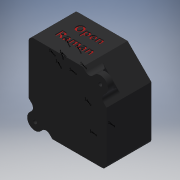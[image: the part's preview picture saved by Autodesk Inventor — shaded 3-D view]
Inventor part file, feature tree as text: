
AUTODESK INVENTOR PART (.ipt)
format: ipt  version: 2017 (Build 210142000, 142)  size: 787,968 bytes
history: native  units: mm
features: sketch x12, extrude x11, other x6, fillet x5, hole x4, projected_geometry x3, chamfer x2
ambient origin geometry x8: Origin, YZ Plane, XZ Plane, XY Plane, X Axis, Y Axis, Z Axis, Center Point
bodies: Body1 (feature_tree)
feature tree (43):
  other  "Blocks"
  other  "OTICA"
  sketch  "Sketch7"  dims[d1=25.4mm d25=0.685475mm]
  extrude  "Extrusion8"  Depth=0.685475mm
  extrude  "Extrusion9"  TaperAngle=112.5deg  [1 undecoded]
  extrude  "Extrusion10"  Depth=10.0mm
  hole  "Hole2"  [1 undecoded]
  extrude  "Extrusion15"  Depth=12.212069mm
  extrude  "Extrusion11"  Depth=11.349876mm
  fillet  "Fillet1"  Radius=10.236356mm
  hole  "Hole3"  [1 undecoded]
  chamfer  "Chamfer1"  Distance=3.154683mm
  hole  "Hole4"  [1 undecoded]
  fillet  "Fillet2"  Radius=20.0mm
  sketch  "Sketch13"  dims[d183=13.325589mm d184=11.349876mm d185=10.236356mm]
  extrude  "Extrusion12"  Depth=10.0mm
  extrude  "Extrusion13"  Depth=10.0mm
  extrude  "Extrusion14"  Depth=10.0mm
  fillet  "Fillet3"  Radius=13.0mm
  extrude  "Extrusion16"  Depth=10.0mm
  extrude  "Extrusion17"  Depth=10.0mm
  fillet  "Fillet4"  Radius=3.529965mm
  fillet  "Fillet5"  Radius=1.293324mm
  extrude  "Extrusion18"  Depth=10.0mm
  chamfer  "Chamfer2"  Angle=90.0deg  [1 undecoded]
  hole  "Hole5"  [1 undecoded]
  other  "PENTAPRISMA"
  other  "PRISMA.ENTRADA"
  sketch  "Sketch8"  dims[d100=3.368863mm d105=3.368863mm d106=6.737727mm d114=90.0deg d115=112.5deg d116=112.5deg d117=112.5deg]
  sketch  "Sketch9"  dims[d118=15.0mm]
  sketch  "Sketch10"  dims[d123=10.78758mm d124=6.58603mm d131=90.0deg d132=5.0mm d133=10.0mm d134=10.0mm d135=45.0deg d136=10.0mm d137=10.0mm d140=7.422885mm d141=6.309365mm d142=3.154683mm]
  sketch  "Sketch11"  dims[d143=3.711443mm d180=13.325589mm]
  projected_geometry  "Projected Loop7"
  projected_geometry  "Projected Loop8"
  sketch  "Sketch12"  dims[d181=12.212069mm d182=12.212069mm]
  sketch  "Sketch14"  dims[d186=11.349876mm d187=10.236356mm]
  projected_geometry  "Projected Loop9"
  sketch  "Sketch15"  dims[d188=29.1mm]
  sketch  "Sketch16"  dims[d189=6.309365mm]
  sketch  "Sketch17"  dims[d190=7.422885mm]
  sketch  "Sketch18"  dims[d191=3.711443mm d192=3.154683mm d195=18.0mm d196=20.0mm d197=4.0mm d198=3.0mm d205=2.0mm d208=13.0mm d209=6.484396mm d210=9.615604mm d211=3.529965mm d212=1.293324mm d213=4.424533mm d214=90.0deg d215=90.0deg d216=21.0mm d217=22.0mm d218=22.0mm d219=22.0mm d220=22.0mm d221=4.0mm d222=40.0mm d223=0.0mm d224=6.0mm d225=0.0mm d226=2.0mm d227=2.0mm d228=2.0mm d229=2.0mm d230=12.0mm d231=0.0mm d232=7.0mm d233=6.0mm d234=12.0mm d235=1.5mm d236=90.0deg d237=5.0mm d238=0.0mm d239=8.0mm d240=6.0mm d241=0.0mm d242=5.0mm d243=4.0mm d244=6.0mm d245=7.0mm d246=2.0mm d247=90.0deg d248=5.0mm d249=0.0mm d250=11.0mm d251=2.0mm d252=45.0deg d253=22.0mm d254=3.0mm d255=6.0mm d256=6.0mm d257=2.0mm d258=90.0deg d259=5.0mm d260=0.0mm d261=5.0mm d262=1.0mm d263=1.0mm d264=1.0mm d265=1.0mm d266=1.0mm d267=1.0mm d268=1.0mm d269=1.0mm d270=1.0mm d271=1.0mm d272=1.0mm d273=5.0mm d274=0.0mm d275=3.0mm d276=0.0mm d277=1.5mm d278=0.0mm d279=2.0mm d280=8.0mm d281=8.0mm d282=3.0mm d283=1.0mm d284=0.3mm d285=0.0mm d286=12.0mm d288=10.0mm d289=0.0mm d290=1.0mm d291=0.0mm d292=1.0mm d293=1.0mm d295=12.0mm d296=0.5mm d297=80.0mm d298=80.0mm d299=0.5mm d300=0.2mm d301=0.0mm d302=0.2mm d303=2.0mm d304=45.0deg d305=46.0mm d306=30.0mm d307=5.0mm d308=5.0mm d309=3.0mm d310=3.0mm d311=3.0mm d312=3.0mm d313=3.0mm d314=6.0mm d315=4.0mm d316=2.0mm d317=90.0deg d318=5.0mm d319=20.594885mm]
  other  "PENTAPRISMA:1"
  other  "PRISMA.ENTRADA:1"
note: 6 required parameter values undecoded (feature->parameter linkage not recoverable at this tier; creation-order binding heuristic only, values carry confidence <= 0.55)
